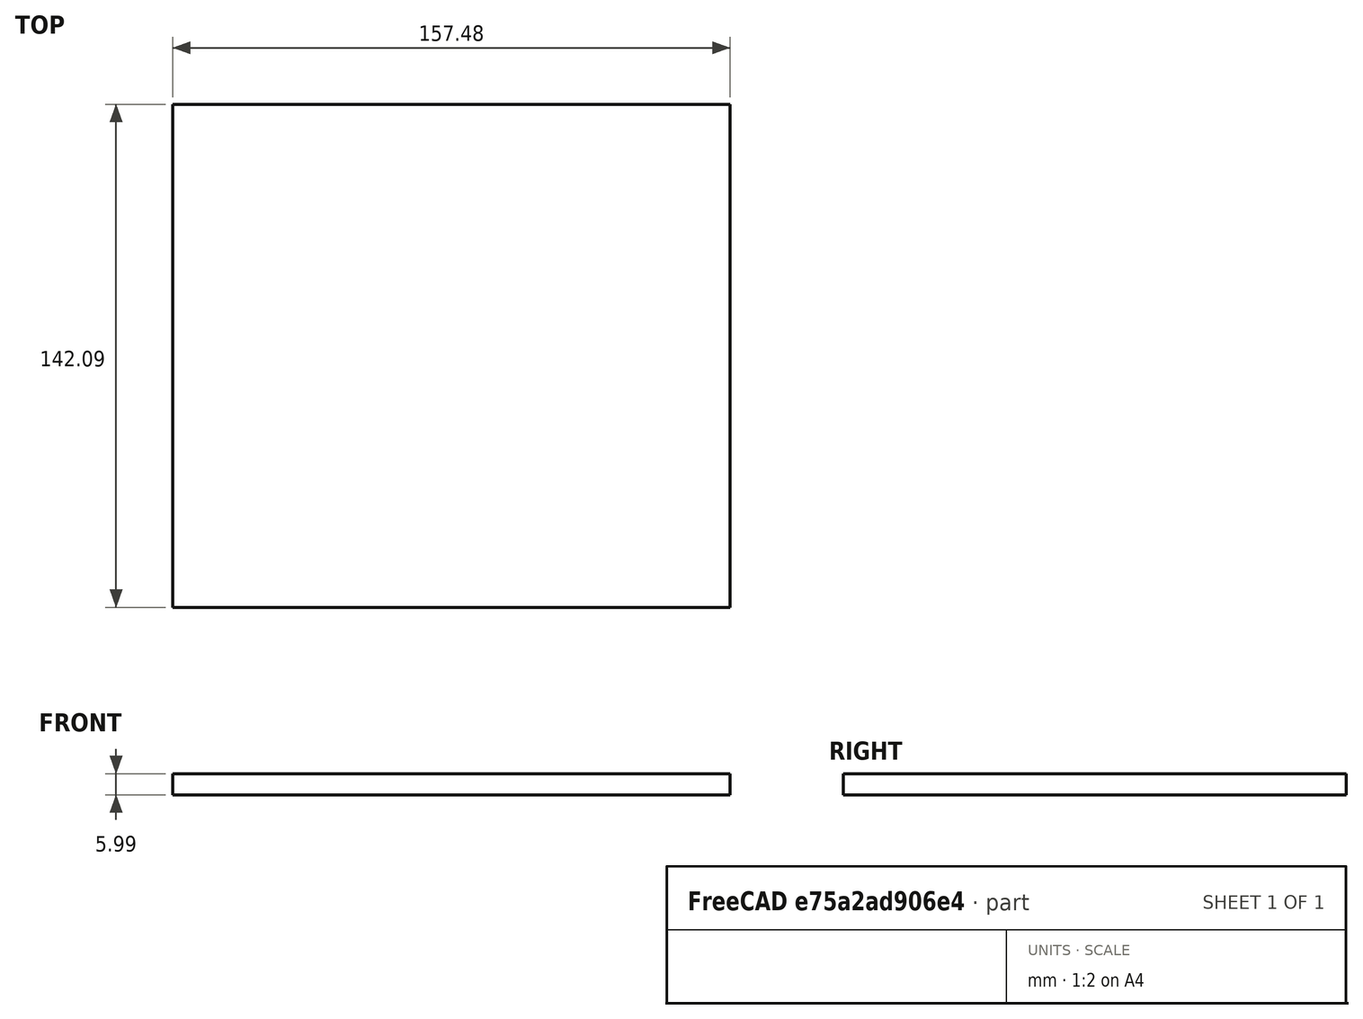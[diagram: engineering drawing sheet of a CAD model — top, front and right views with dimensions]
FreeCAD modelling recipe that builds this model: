
FCSTD DOCUMENT  (FreeCAD 0.19R24267 (Git))
Label: Inv1-P11
License: All rights reserved
LicenseURL: http://en.wikipedia.org/wiki/All_rights_reserved
objects: TechDraw::DrawViewDimension×3, TechDraw::DrawProjGroupItem×2, TechDraw::DrawHatch×2, TechDraw::DrawViewAnnotation×2, Sketcher::SketchObject×1, Part::Extrusion×1, TechDraw::DrawSVGTemplate×1, TechDraw::DrawProjGroup×1, TechDraw::DrawPage×1
note: 2 computed .brp shape members not serialized (recipe doc carries the construction recipe); baked Part::Feature solids carry a one-line shape summary decoded from their .brp

FEATURE [Sketcher::SketchObject] Sketch
  FullyConstrained = false
  sketch-geometry (4):
    g0: LineSegment StartX=-99.9457 StartY=47.7317 StartZ=0 EndX=57.5343 EndY=47.7317 EndZ=0
    g1: LineSegment StartX=57.5343 StartY=47.7317 StartZ=0 EndX=57.5343 EndY=-94.3559 EndZ=0
    g2: LineSegment StartX=57.5343 StartY=-94.3559 StartZ=0 EndX=-99.9457 EndY=-94.3559 EndZ=0
    g3: LineSegment StartX=-99.9457 StartY=-94.3559 StartZ=0 EndX=-99.9457 EndY=47.7317 EndZ=0
  constraints (10):
    c: Coincident(g0,g1)
    c: Coincident(g1,g2)
    c: Coincident(g2,g3)
    c: Coincident(g3,g0)
    c: Horizontal(g0)
    c: Horizontal(g2)
    c: Vertical(g1)
    c: Vertical(g3)
    c: DistanceY(g3,g3) = 142.088
    c: DistanceX(g0,g0) = 157.48
FEATURE [Part::Extrusion] Extrude
  Base = -> Sketch
  Dir = (0,0,1)
  DirMode = 2
  FaceMakerClass = Part::FaceMakerBullseye
  LengthFwd = 5.9944
  LengthRev = 0
  Solid = true
  Symmetric = false
FEATURE [TechDraw::DrawSVGTemplate] Template
  Height = 215.9
  Orientation = 1
  Width = 279.4
FEATURE [TechDraw::DrawProjGroupItem] ProjItem  label="Front"
  CoarseView = false
  Direction = (0,0,1)
  Focus = 100
  HardHidden = false
  IsoCount = 0
  IsoHidden = false
  IsoVisible = false
  LockPosition = true
  Perspective = false
  Rotation = 0
  RotationVector = (1,0,0)
  Scale = 0.5
  ScaleType = 2
  SeamHidden = false
  SeamVisible = true
  SmoothHidden = false
  SmoothVisible = true
  Source = -> [Extrude]
  Type = 0
  X = 0
  XDirection = (1,0,0)
  Y = 0
FEATURE [TechDraw::DrawProjGroupItem] ProjItem001  label="Left"
  CoarseView = false
  Direction = (-1,0,1e-16)
  Focus = 100
  HardHidden = false
  IsoCount = 0
  IsoHidden = false
  IsoVisible = false
  LockPosition = false
  Perspective = false
  Rotation = 0
  RotationVector = (1,0,0)
  Scale = 0.5
  ScaleType = 2
  SeamHidden = false
  SeamVisible = true
  SmoothHidden = false
  SmoothVisible = true
  Source = -> [Extrude]
  Type = 1
  X = 72.8733
  XDirection = (1e-16,0,1)
  Y = 0
FEATURE [TechDraw::DrawProjGroup] ProjGroup
  Anchor = -> ProjItem
  AutoDistribute = true
  LockPosition = false
  ProjectionType = 0
  Rotation = 0
  Scale = 0.5
  ScaleType = 2
  Source = -> [Extrude]
  Views = -> [ProjItem,ProjItem001]
  X = 127.783
  Y = 110.157
  spacingX = 15.0114
  spacingY = 15.0114
FEATURE [TechDraw::DrawHatch] Hatch  label="HatchF0"
  HatchPattern = <path>
  Source = -> ProjItem [Face0]
FEATURE [TechDraw::DrawHatch] Hatch001  label="Hatch001F0"
  HatchPattern = <path>
  Source = -> ProjItem001 [Face0]
FEATURE [TechDraw::DrawViewDimension] Dimension
  Arbitrary = false
  ArbitraryTolerances = false
  EqualTolerance = true
  FormatSpec = %.3f
  FormatSpecOverTolerance = %+.3f
  FormatSpecUnderTolerance = %+.3f
  Inverted = false
  LockPosition = false
  MeasureType = 1
  OverTolerance = 0
  References2D = -> [ProjItem]
  Rotation = 0
  ScaleType = 0
  TheoreticalExact = false
  Type = 1
  UnderTolerance = 0
  X = -0.882726
  Y = -46.9973
FEATURE [TechDraw::DrawViewDimension] Dimension001
  Arbitrary = false
  ArbitraryTolerances = false
  EqualTolerance = true
  FormatSpec = %.3f
  FormatSpecOverTolerance = %+.3f
  FormatSpecUnderTolerance = %+.3f
  Inverted = false
  LockPosition = false
  MeasureType = 1
  OverTolerance = 0
  References2D = -> [ProjItem]
  Rotation = 0
  ScaleType = 0
  TheoreticalExact = false
  Type = 2
  UnderTolerance = 0
  X = 47.3145
  Y = -1.32409
FEATURE [TechDraw::DrawViewDimension] Dimension002
  Arbitrary = false
  ArbitraryTolerances = false
  EqualTolerance = true
  FormatSpec = %.3f
  FormatSpecOverTolerance = %+.3f
  FormatSpecUnderTolerance = %+.3f
  Inverted = false
  LockPosition = false
  MeasureType = 1
  OverTolerance = 0
  References2D = -> [ProjItem001]
  Rotation = 0
  ScaleType = 0
  TheoreticalExact = false
  Type = 1
  UnderTolerance = 0
  X = 22.1717
  Y = 27.1853
FEATURE [TechDraw::DrawViewAnnotation] Annotation
  Font = osifont
  LineSpace = 80
  LockPosition = false
  MaxWidth = -1
  Rotation = 0
  ScaleType = 0
  Text = Figure S1 (Inverted 1) | Panel 11 [focus pocket back left] | Quantity: 1
  TextSize = 5.0038
  TextStyle = 0
  X = 44.6733
  Y = 195.58
FEATURE [TechDraw::DrawViewAnnotation] Annotation002
  Font = osifont
  LineSpace = 80
  LockPosition = false
  MaxWidth = -1
  Rotation = 0
  ScaleType = 0
  Text = Units: Inches
  TextSize = 5.0038
  TextStyle = 0
  X = 259.08
  Y = 5.08
FEATURE [TechDraw::DrawPage] Page
  KeepUpdated = true
  NextBalloonIndex = 1
  ProjectionType = 0
  Template = -> Template
  Views = -> [ProjGroup,Dimension,Dimension001,Dimension002,Annotation,Annotation002]
note: 2 file-system paths scrubbed to <path> (originals preserved in the JSON sidecar)
